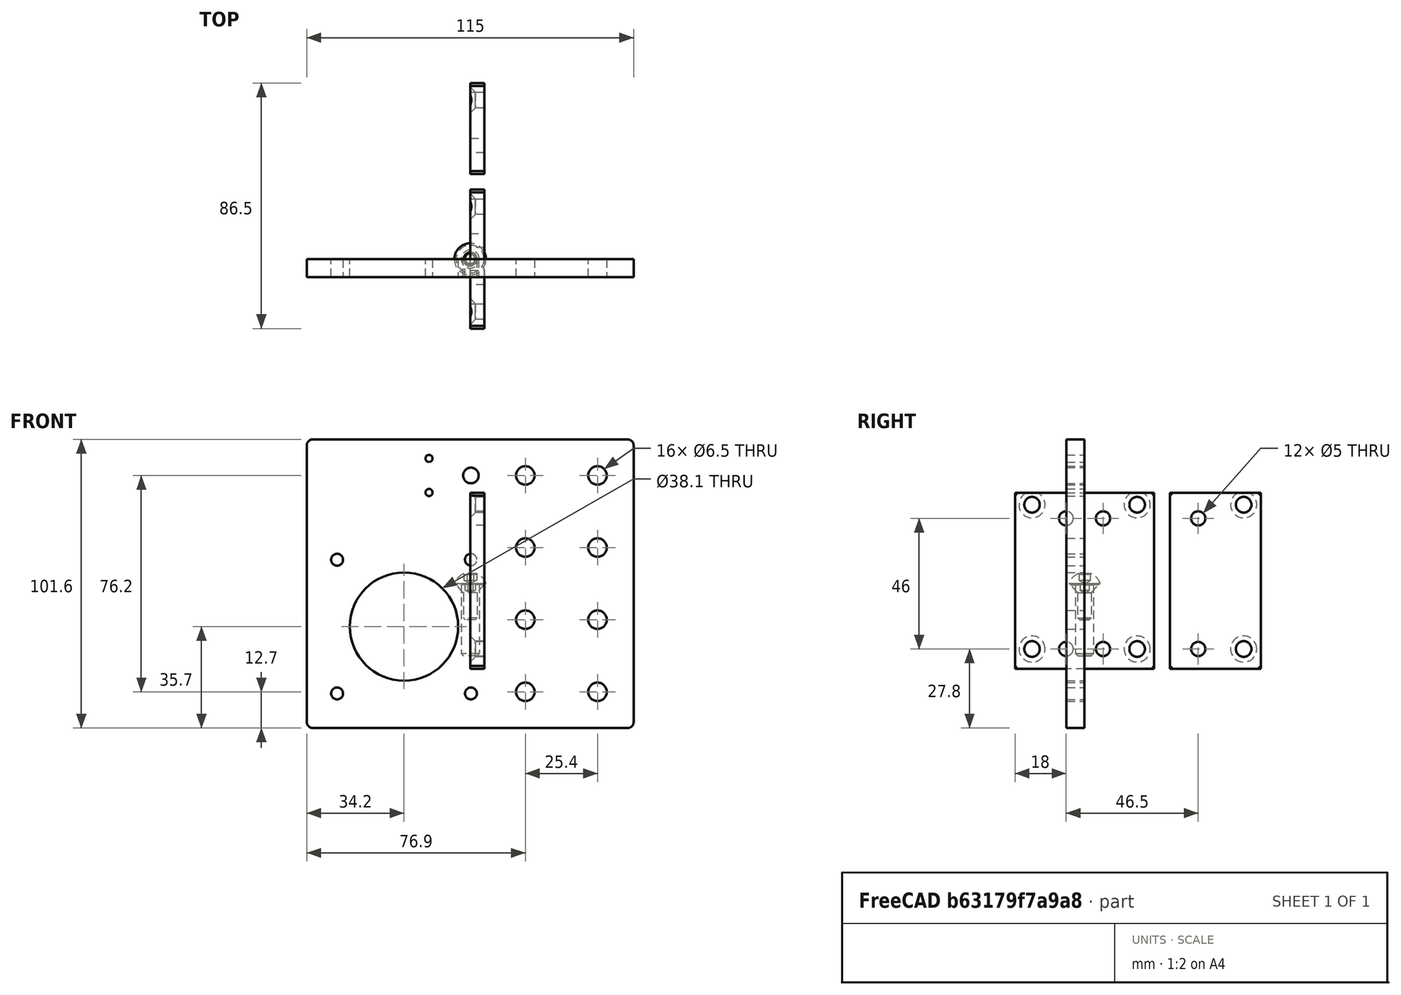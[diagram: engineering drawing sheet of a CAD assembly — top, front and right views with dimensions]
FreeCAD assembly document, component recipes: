
FREECAD ASSEMBLY — COMPONENT RECIPES ("Y axis plates")

This assembly document has 18 components, labeled P0..P17 below (a component is one placed body or linked part). 10 of them carry a construction recipe — the FreeCAD feature program that regenerates the part from scratch, quoted from this document or its linked companion documents; the rest are supplied as boundary geometry only. No exploded tour is included for this assembly.
COMPONENT P0 — recipe-attached ("BK12 plate", modeled in this document).
Construction recipe (the document's own serialized feature program — sketch geometry with constraints, then the solid features built on it; lengths are millimeters unless a unit is written):

FEATURE [Sketcher::SketchObject] Sketch
  FullyConstrained = true
  MapMode = 5
  Placement = pos=(0,0,0) rot=(0.57735,0.57735,0.57735;2.0944rad)
  Support = -> [YZ_Plane]
  sketch-geometry (16):
    g0: LineSegment StartX=-24.5 StartY=32 StartZ=0 EndX=24.5 EndY=32 EndZ=0
    g1: LineSegment StartX=24.5 StartY=32 StartZ=0 EndX=24.5 EndY=-30 EndZ=0
    g2: LineSegment StartX=24.5 StartY=-30 StartZ=0 EndX=-24.5 EndY=-30 EndZ=0
    g3: LineSegment StartX=-24.5 StartY=-30 StartZ=0 EndX=-24.5 EndY=32 EndZ=0
    g4: LineSegment [constr] StartX=-12.5 StartY=30 StartZ=0 EndX=12.5 EndY=30 EndZ=0
    g5: LineSegment [constr] StartX=12.5 StartY=30 StartZ=0 EndX=12.5 EndY=-30 EndZ=0
    g6: LineSegment [constr] StartX=12.5 StartY=-30 StartZ=0 EndX=-12.5 EndY=-30 EndZ=0
    g7: LineSegment [constr] StartX=-12.5 StartY=-30 StartZ=0 EndX=-12.5 EndY=30 EndZ=0
    g8: Circle CenterX=-6.5 CenterY=23 CenterZ=0 NormalX=0 NormalY=0 NormalZ=1 AngleXU=0 Radius=2.5
    g9: Circle CenterX=6.5 CenterY=23 CenterZ=0 NormalX=0 NormalY=0 NormalZ=1 AngleXU=0 Radius=2.5
    g10: Circle CenterX=-6.5 CenterY=-23 CenterZ=0 NormalX=0 NormalY=0 NormalZ=1 AngleXU=0 Radius=2.5
    g11: Circle CenterX=6.5 CenterY=-23 CenterZ=0 NormalX=0 NormalY=0 NormalZ=1 AngleXU=0 Radius=2.5
    g12: Circle CenterX=18.5 CenterY=-23 CenterZ=0 NormalX=0 NormalY=0 NormalZ=1 AngleXU=0 Radius=2.75
    g13: Circle CenterX=18.5 CenterY=27.8 CenterZ=0 NormalX=0 NormalY=0 NormalZ=1 AngleXU=0 Radius=2.75
    g14: Circle CenterX=-18.5 CenterY=27.8 CenterZ=0 NormalX=0 NormalY=0 NormalZ=1 AngleXU=0 Radius=2.75
    g15: Circle CenterX=-18.5 CenterY=-23 CenterZ=0 NormalX=0 NormalY=0 NormalZ=1 AngleXU=0 Radius=2.75
  constraints (44):
    c: Coincident(g0,g1)
    c: Coincident(g1,g2)
    c: Coincident(g2,g3)
    c: Coincident(g3,g0)
    c: Horizontal(g0)
    c: Vertical(g1)
    c: Vertical(g3)
    c: Coincident(g4,g5)
    c: Coincident(g5,g6)
    c: Coincident(g6,g7)
    c: Coincident(g7,g4)
    c: Horizontal(g4)
    c: Horizontal(g6)
    c: Vertical(g5)
    c: Vertical(g7)
    c: Symmetric(g5,g4,g-1)
    c: DistanceY(g5,g5) = 60
    c: DistanceX(g4,g4) = 25
    c: Symmetric(g8,g11,g-1)
    c: Vertical(g8,g10)
    c: Vertical(g9,g11)
    c: Horizontal(g8,g9)
    c: Horizontal(g10,g11)
    c: Equal(g8,g9)
    c: Diameter(g9) = 5
    c: DistanceX(g10,g11) = 13
    c: DistanceY(g11,g9) = 46
    c: Horizontal(g2,g6)
    c: DistanceX(g4,g13) = 6
    c: DistanceX(g13,g0) = 6
    c: DistanceY(g12,g13) = 50.8
    c: Equal(g13,g12)
    c: Diameter(g13) = 5.5
    c: Vertical(g12,g13)
    c: Horizontal(g11,g12)
    c: Symmetric(g1,g2,g-2)
    c: Equal(g15,g14)
    c: Equal(g14,g13)
    c: Horizontal(g14,g13)
    c: Symmetric(g12,g15,g-2)
    c: Vertical(g14,g15)
    c: Equal(g10,g11)
    c: Equal(g10,g8)
    c: DistanceY(g3,g3) = 62
FEATURE [PartDesign::Pad] Pad
  ClaimChildren = false
  Direction = (1,1,1)
  Fit = 0
  FitJoin = 0
  InnerFit = 0
  InnerFitJoin = 0
  InnerTaperAngle = 0
  InnerTaperAngleRev = 0
  Length = 5
  Length2 = 100
  Linearize = true
  NewSolid = false
  Placement = pos=(0,0,0) rot=(0.57735,0.57735,0.57735;2.0944rad)
  Profile = -> Sketch
  Refine = true
  Suppress = false
  Type = 0
  _ProfileBasedVersion = 0
FEATURE [PartDesign::Body] Body  label="BK12 plate"
  AutoGroupSolids = false
  ExportMode = 0
  Group = -> [Sketch,Pad]
  Origin = -> Origin
  Tip = -> Pad
  _ExportChildren = -> [Pad]
  _GroupVersion = 1
COMPONENT P1 — recipe-attached ("BF12 plate", modeled in this document).
Construction recipe (the document's own serialized feature program — sketch geometry with constraints, then the solid features built on it; lengths are millimeters unless a unit is written):

FEATURE [Sketcher::SketchObject] Sketch001
  FullyConstrained = true
  MapMode = 5
  Placement = pos=(0,0,0) rot=(0.57735,0.57735,0.57735;2.0944rad)
  Support = -> [YZ_Plane001]
  sketch-geometry (12):
    g0: LineSegment [constr] StartX=-10 StartY=30 StartZ=0 EndX=10 EndY=30 EndZ=0
    g1: LineSegment [constr] StartX=10 StartY=30 StartZ=0 EndX=10 EndY=-30 EndZ=0
    g2: LineSegment [constr] StartX=10 StartY=-30 StartZ=0 EndX=-10 EndY=-30 EndZ=0
    g3: LineSegment [constr] StartX=-10 StartY=-30 StartZ=0 EndX=-10 EndY=30 EndZ=0
    g4: Circle CenterX=0 CenterY=23 CenterZ=0 NormalX=0 NormalY=0 NormalZ=1 AngleXU=0 Radius=2.5
    g5: Circle CenterX=0 CenterY=-23 CenterZ=0 NormalX=0 NormalY=0 NormalZ=1 AngleXU=0 Radius=2.5
    g6: Circle CenterX=16 CenterY=27.8 CenterZ=0 NormalX=0 NormalY=0 NormalZ=1 AngleXU=0 Radius=2.75
    g7: Circle CenterX=16 CenterY=-23 CenterZ=0 NormalX=0 NormalY=0 NormalZ=1 AngleXU=0 Radius=2.75
    g8: LineSegment StartX=-10 StartY=-30 StartZ=0 EndX=22 EndY=-30 EndZ=0
    g9: LineSegment StartX=22 StartY=-30 StartZ=0 EndX=22 EndY=32 EndZ=0
    g10: LineSegment StartX=22 StartY=32 StartZ=0 EndX=-10 EndY=32 EndZ=0
    g11: LineSegment StartX=-10 StartY=32 StartZ=0 EndX=-10 EndY=-30 EndZ=0
  constraints (33):
    c: Coincident(g0,g1)
    c: Coincident(g1,g2)
    c: Coincident(g2,g3)
    c: Coincident(g3,g0)
    c: Horizontal(g0)
    c: Horizontal(g2)
    c: Vertical(g1)
    c: Vertical(g3)
    c: Symmetric(g1,g0,g-1)
    c: DistanceX(g0,g0) = 20
    c: DistanceY(g1,g1) = 60
    c: PointOnObject(g4,g-2)
    c: Symmetric(g5,g4,g-1)
    c: DistanceY(g5,g4) = 46
    c: Diameter(g4) = 5
    c: Diameter(g7) = 5.5
    c: Equal(g7,g6)
    c: Horizontal(g7,g5)
    c: Vertical(g7,g6)
    c: DistanceY(g7,g6) = 50.8
    c: DistanceX(g0,g6) = 6
    c: Coincident(g8,g9)
    c: Coincident(g9,g10)
    c: Coincident(g10,g11)
    c: Coincident(g11,g8)
    c: Horizontal(g8)
    c: Horizontal(g10)
    c: Vertical(g9)
    c: Vertical(g11)
    c: Coincident(g8,g2)
    c: DistanceX(g6,g9) = 6
    c: Equal(g5,g4)
    c: DistanceY(g9,g9) = 62
FEATURE [PartDesign::Pad] Pad001
  ClaimChildren = false
  Direction = (1,1,1)
  Fit = 0
  FitJoin = 0
  InnerFit = 0
  InnerFitJoin = 0
  InnerTaperAngle = 0
  InnerTaperAngleRev = 0
  Length = 5
  Length2 = 100
  Linearize = true
  NewSolid = false
  Placement = pos=(0,0,0) rot=(0.57735,0.57735,0.57735;2.0944rad)
  Profile = -> Sketch001
  Refine = true
  Suppress = false
  Type = 0
  _ProfileBasedVersion = 0
FEATURE [PartDesign::Body] Body001  label="BF12 plate"
  AutoGroupSolids = false
  ExportMode = 0
  Group = -> [Sketch001,Pad001]
  Origin = -> Origin001
  Placement = pos=(0,40,0) rot=(0,0,1;0rad)
  Tip = -> Pad001
  _ExportChildren = -> [Pad001]
  _GroupVersion = 1
COMPONENT P2 — recipe-attached ("Link(BK12R plate)", modeled in this document).
Construction recipe (the document's own serialized feature program — sketch geometry with constraints, then the solid features built on it; lengths are millimeters unless a unit is written):

FEATURE [PartDesign::SubShapeBinder] BaseFeature002  label="BaseFeature002(BK12 plate)"
  BindCopyOnChange = 0
  BindMode = 0
  ClaimChildren = false
  Context = -> Body004 [BaseFeature002.]
  FillStyle = 0
  Fuse = true
  MakeFace = true
  PartialLoad = false
  Relative = true
  Support = -> [Body]
  _Version = 8
FEATURE [PartDesign::Chamfer] Chamfer002
  Angle = 45
  Base = -> BaseFeature002 [Edge2,Edge1,Edge5,Edge8]
  ChamferType = 0
  FlipDirection = false
  NewSolid = false
  Refine = true
  Size = 1
  Size2 = 1
  SupportTransform = false
  Suppress = false
FEATURE [PartDesign::Hole] Hole002
  BaseFeature = -> Chamfer002
  ClaimChildren = false
  CustomThreadClearance = 0
  Depth = 25
  DepthType = 0
  Diameter = 5.5
  DrillForDepth = false
  DrillPoint = 1
  DrillPointAngle = 118
  Fit = 0
  FitJoin = 0
  HoleCutCountersinkAngle = 90
  HoleCutCustomValues = false
  HoleCutDepth = 0
  HoleCutDiameter = 9.2
  HoleCutType = 2
  InnerFit = 0
  InnerFitJoin = 0
  ModelThread = false
  NewSolid = false
  Profile = -> Chamfer002 [Edge29,Edge32,Edge31,Edge30]
  Refine = true
  Suppress = false
  Tapered = false
  TaperedAngle = 90
  ThreadClass = 0
  ThreadDepth = 23.5
  ThreadDepthType = 0
  ThreadDirection = 0
  ThreadFit = 0
  ThreadSize = 0
  ThreadType = 0
  Threaded = false
  UseCustomThreadClearance = false
  _ProfileBasedVersion = 0
FEATURE [PartDesign::Body] Body004  label="BK12R plate"
  AutoGroupSolids = false
  BaseFeature = -> BaseFeature002
  ExportMode = 0
  Group = -> [BaseFeature002,Chamfer002,Hole002]
  Origin = -> Origin004
  Tip = -> Hole002
  _ExportChildren = -> [BaseFeature002,Hole002]
  _GroupVersion = 1
COMPONENT P3 — recipe-attached ("Link001(BK12L plate)", modeled in this document).
Construction recipe (the document's own serialized feature program — sketch geometry with constraints, then the solid features built on it; lengths are millimeters unless a unit is written):

FEATURE [PartDesign::SubShapeBinder] BaseFeature003  label="BaseFeature003(BK12 plate)"
  BindCopyOnChange = 0
  BindMode = 0
  ClaimChildren = false
  Context = -> Body005 [BaseFeature003.]
  FillStyle = 0
  Fuse = true
  MakeFace = true
  PartialLoad = false
  Relative = true
  Support = -> [Body]
  _Version = 8
FEATURE [PartDesign::Chamfer] Chamfer003
  Angle = 45
  Base = -> BaseFeature003 [Edge2,Edge1,Edge8,Edge5]
  ChamferType = 0
  FlipDirection = false
  NewSolid = false
  Refine = true
  Size = 1
  Size2 = 1
  SupportTransform = false
  Suppress = false
FEATURE [PartDesign::Hole] Hole003
  BaseFeature = -> Chamfer003
  ClaimChildren = false
  CustomThreadClearance = 0
  Depth = 25
  DepthType = 0
  Diameter = 5.5
  DrillForDepth = false
  DrillPoint = 1
  DrillPointAngle = 118
  Fit = 0
  FitJoin = 0
  HoleCutCountersinkAngle = 90
  HoleCutCustomValues = false
  HoleCutDepth = 0
  HoleCutDiameter = 9.2
  HoleCutType = 2
  InnerFit = 0
  InnerFitJoin = 0
  ModelThread = false
  NewSolid = false
  Profile = -> Chamfer003 [Edge12,Edge15,Edge14,Edge13]
  Refine = true
  Reversed = true
  Suppress = false
  Tapered = false
  TaperedAngle = 90
  ThreadClass = 0
  ThreadDepth = 23.5
  ThreadDepthType = 0
  ThreadDirection = 0
  ThreadFit = 0
  ThreadSize = 0
  ThreadType = 0
  Threaded = false
  UseCustomThreadClearance = false
  _ProfileBasedVersion = 0
FEATURE [PartDesign::Body] Body005  label="BK12L plate"
  AutoGroupSolids = false
  BaseFeature = -> BaseFeature003
  ExportMode = 0
  Group = -> [BaseFeature003,Chamfer003,Hole003]
  Origin = -> Origin005
  Tip = -> Hole003
  _ExportChildren = -> [BaseFeature003,Hole003]
  _GroupVersion = 1
COMPONENT P4 — recipe-attached ("Link002(BF12L plate)", modeled in this document).
Construction recipe (the document's own serialized feature program — sketch geometry with constraints, then the solid features built on it; lengths are millimeters unless a unit is written):

FEATURE [PartDesign::SubShapeBinder] BaseFeature001  label="BaseFeature001(BF12 plate)"
  BindCopyOnChange = 0
  BindMode = 0
  ClaimChildren = false
  Context = -> Body003 [BaseFeature001.]
  FillStyle = 0
  Fuse = true
  MakeFace = true
  PartialLoad = false
  Relative = true
  Support = -> [Body001]
  _Version = 8
FEATURE [PartDesign::Chamfer] Chamfer001
  Angle = 45
  Base = -> BaseFeature001 [Edge5,Edge8,Edge2,Edge1]
  ChamferType = 0
  FlipDirection = false
  NewSolid = false
  Refine = true
  Size = 1
  Size2 = 1
  SupportTransform = false
  Suppress = false
FEATURE [PartDesign::Hole] Hole001
  BaseFeature = -> Chamfer001
  ClaimChildren = false
  CustomThreadClearance = 0
  Depth = 25
  DepthType = 0
  Diameter = 5.5
  DrillForDepth = false
  DrillPoint = 1
  DrillPointAngle = 118
  Fit = 0
  FitJoin = 0
  HoleCutCountersinkAngle = 90
  HoleCutCustomValues = false
  HoleCutDepth = 0
  HoleCutDiameter = 9.2
  HoleCutType = 2
  InnerFit = 0
  InnerFitJoin = 0
  ModelThread = false
  NewSolid = false
  Profile = -> Chamfer001 [Edge13,Edge12]
  Refine = true
  Reversed = true
  Suppress = false
  Tapered = false
  TaperedAngle = 90
  ThreadClass = 0
  ThreadDepth = 23.5
  ThreadDepthType = 0
  ThreadDirection = 0
  ThreadFit = 0
  ThreadSize = 0
  ThreadType = 0
  Threaded = false
  UseCustomThreadClearance = false
  _ProfileBasedVersion = 0
FEATURE [PartDesign::Body] Body003  label="BF12L plate"
  AutoGroupSolids = false
  BaseFeature = -> BaseFeature001
  ExportMode = 0
  Group = -> [BaseFeature001,Chamfer001,Hole001]
  Origin = -> Origin003
  Tip = -> Hole001
  _ExportChildren = -> [BaseFeature001,Hole001]
  _GroupVersion = 1
COMPONENT P5 — recipe-attached ("Link003(BF12R plate)", modeled in this document).
Construction recipe (the document's own serialized feature program — sketch geometry with constraints, then the solid features built on it; lengths are millimeters unless a unit is written):

FEATURE [PartDesign::SubShapeBinder] BaseFeature  label="BaseFeature(BF12 plate)"
  BindCopyOnChange = 0
  BindMode = 0
  ClaimChildren = false
  Context = -> Body002 [BaseFeature.]
  FillStyle = 0
  Fuse = true
  MakeFace = true
  PartialLoad = false
  Relative = true
  Support = -> [Body001]
  _Version = 8
FEATURE [PartDesign::Chamfer] Chamfer
  Angle = 45
  Base = -> BaseFeature [Edge5,Edge8,Edge2,Edge1]
  ChamferType = 0
  FlipDirection = false
  NewSolid = false
  Refine = true
  Size = 1
  Size2 = 1
  SupportTransform = false
  Suppress = false
FEATURE [PartDesign::Hole] Hole
  BaseFeature = -> Chamfer
  ClaimChildren = false
  CustomThreadClearance = 0
  Depth = 25
  DepthType = 0
  Diameter = 5.5
  DrillForDepth = false
  DrillPoint = 1
  DrillPointAngle = 118
  Fit = 0
  FitJoin = 0
  HoleCutCountersinkAngle = 90
  HoleCutCustomValues = false
  HoleCutDepth = 0
  HoleCutDiameter = 9.2
  HoleCutType = 2
  InnerFit = 0
  InnerFitJoin = 0
  ModelThread = false
  NewSolid = false
  Profile = -> Chamfer [Edge26,Edge25]
  Refine = true
  Suppress = false
  Tapered = false
  TaperedAngle = 90
  ThreadClass = 0
  ThreadDepth = 23.5
  ThreadDepthType = 0
  ThreadDirection = 0
  ThreadFit = 0
  ThreadSize = 0
  ThreadType = 0
  Threaded = false
  UseCustomThreadClearance = false
  _ProfileBasedVersion = 0
FEATURE [PartDesign::Body] Body002  label="BF12R plate"
  AutoGroupSolids = false
  BaseFeature = -> BaseFeature
  ExportMode = 0
  Group = -> [BaseFeature,Chamfer,Hole]
  Origin = -> Origin002
  Tip = -> Hole
  _ExportChildren = -> [BaseFeature,Hole]
  _GroupVersion = 1
COMPONENT P6 — recipe-attached ("Link004(motor plate)", modeled in this document).
Construction recipe (the document's own serialized feature program — sketch geometry with constraints, then the solid features built on it; lengths are millimeters unless a unit is written):

FEATURE [Sketcher::SketchObject] Sketch002
  FullyConstrained = true
  MapMode = 5
  Placement = pos=(0,0,0) rot=(1,0,0;1.5708rad)
  Support = -> [XZ_Plane006]
  sketch-geometry (23):
    g0: LineSegment StartX=-57.5 StartY=50.8 StartZ=0 EndX=57.5 EndY=50.8 EndZ=0
    g1: LineSegment StartX=57.5 StartY=50.8 StartZ=0 EndX=57.5 EndY=-50.8 EndZ=0
    g2: LineSegment StartX=57.5 StartY=-50.8 StartZ=0 EndX=-57.5 EndY=-50.8 EndZ=0
    g3: LineSegment StartX=-57.5 StartY=-50.8 StartZ=0 EndX=-57.5 EndY=50.8 EndZ=0
    g4: Circle CenterX=19.4 CenterY=38.1 CenterZ=0 NormalX=0 NormalY=0 NormalZ=1 AngleXU=0 Radius=3.25
    g5: Circle CenterX=44.8 CenterY=38.1 CenterZ=0 NormalX=0 NormalY=0 NormalZ=1 AngleXU=0 Radius=3.25
    g6: Circle CenterX=19.4 CenterY=12.7 CenterZ=0 NormalX=0 NormalY=0 NormalZ=1 AngleXU=0 Radius=3.25
    g7: Circle CenterX=44.8 CenterY=12.7 CenterZ=0 NormalX=0 NormalY=0 NormalZ=1 AngleXU=0 Radius=3.25
    g8: Circle CenterX=19.4 CenterY=-12.7 CenterZ=0 NormalX=0 NormalY=0 NormalZ=1 AngleXU=0 Radius=3.25
    g9: Circle CenterX=44.8 CenterY=-12.7 CenterZ=0 NormalX=0 NormalY=0 NormalZ=1 AngleXU=0 Radius=3.25
    g10: Circle CenterX=19.4 CenterY=-38.1 CenterZ=0 NormalX=0 NormalY=0 NormalZ=1 AngleXU=0 Radius=3.25
    g11: Circle CenterX=44.8 CenterY=-38.1 CenterZ=0 NormalX=0 NormalY=0 NormalZ=1 AngleXU=0 Radius=3.25
    g12: LineSegment [constr] StartX=19.4 StartY=38.1 StartZ=0 EndX=44.8 EndY=38.1 EndZ=0
    g13: LineSegment [constr] StartX=19.4 StartY=38.1 StartZ=0 EndX=19.4 EndY=12.7 EndZ=0
    g14: LineSegment [constr] StartX=19.4 StartY=12.7 StartZ=0 EndX=19.4 EndY=-12.7 EndZ=0
    g15: LineSegment [constr] StartX=19.4 StartY=-12.7 StartZ=0 EndX=19.4 EndY=-38.1 EndZ=0
    g16: Circle CenterX=-23.3 CenterY=-15.1 CenterZ=0 NormalX=0 NormalY=0 NormalZ=1 AngleXU=0 Radius=19.05
    g17: Circle CenterX=-46.85 CenterY=8.45 CenterZ=0 NormalX=0 NormalY=0 NormalZ=1 AngleXU=0 Radius=2.1
    g18: Circle CenterX=0.25 CenterY=8.45 CenterZ=0 NormalX=0 NormalY=0 NormalZ=1 AngleXU=0 Radius=2.1
    g19: Circle CenterX=-46.85 CenterY=-38.65 CenterZ=0 NormalX=0 NormalY=0 NormalZ=1 AngleXU=0 Radius=2.1
    g20: Circle CenterX=0.25 CenterY=-38.65 CenterZ=0 NormalX=0 NormalY=0 NormalZ=1 AngleXU=0 Radius=2.1
    g21: LineSegment [constr] StartX=-46.85 StartY=8.45 StartZ=0 EndX=0.25 EndY=8.45 EndZ=0
    g22: LineSegment [constr] StartX=-46.85 StartY=8.45 StartZ=0 EndX=-46.85 EndY=-38.65 EndZ=0
  constraints (56):
    c: Coincident(g0,g1)
    c: Coincident(g1,g2)
    c: Coincident(g2,g3)
    c: Coincident(g3,g0)
    c: Horizontal(g0)
    c: Horizontal(g2)
    c: Vertical(g1)
    c: Vertical(g3)
    c: DistanceX(g0,g0) = 115
    c: DistanceY(g1,g1) = 101.6
    c: Symmetric(g2,g0,g-1)
    c: Diameter(g4) = 6.5
    c: Equal(g4, g5-g9) x5
    c: Equal(g4,g11)
    c: Equal(g4,g10)
    c: Vertical(g4,g6)
    c: Vertical(g8,g10)
    c: Vertical(g5,g7)
    c: Vertical(g7,g9)
    c: Vertical(g9,g11)
    c: Horizontal(g10,g11)
    c: Horizontal(g4,g5)
    c: Horizontal(g6,g7)
    c: Horizontal(g8,g9)
    c: DistanceX(g5,g0) = 12.7
    c: Coincident(g12,g4)
    c: Coincident(g12,g5)
    c: Coincident(g13,g4)
    c: Coincident(g13,g6)
    c: Coincident(g14,g6)
    c: Coincident(g14,g8)
    c: Coincident(g15,g8)
    c: Coincident(g15,g10)
    c: Equal(g15,g14)
    c: Equal(g14,g13)
    c: Equal(g13,g12)
    c: DistanceX(g10,g11) = 25.4
    c: Symmetric(g6,g8,g-1)
    c: Horizontal(g20,g19)
    c: Horizontal(g17,g18)
    c: Vertical(g18,g20)
    c: Vertical(g17,g19)
    c: Diameter(g19) = 4.2
    c: Equal(g19,g20)
    c: Equal(g19,g18)
    c: Equal(g19,g17)
    c: Symmetric(g19,g18,g16)
    c: Diameter(g16) = 38.1
    c: Coincident(g21,g17)
    c: Coincident(g21,g18)
    c: Coincident(g22,g17)
    c: Coincident(g22,g19)
    c: Equal(g22,g21)
    c: DistanceX(g21,g21) = 47.1
    c: DistanceY(g10,g16) = 23
    c: DistanceX(g16,g10) = 42.7
FEATURE [PartDesign::Pad] Pad002
  ClaimChildren = false
  Direction = (1,1,1)
  Fit = 0
  FitJoin = 0
  InnerFit = 0
  InnerFitJoin = 0
  InnerTaperAngle = 0
  InnerTaperAngleRev = 0
  Length = 6.35
  Length2 = 100
  Linearize = true
  NewSolid = false
  Placement = pos=(0,0,0) rot=(1,0,0;1.5708rad)
  Profile = -> Sketch002
  Refine = true
  Suppress = false
  Type = 0
  _ProfileBasedVersion = 0
FEATURE [PartDesign::Fillet] Fillet
  Base = -> Pad002 [Edge2,Edge5,Edge8,Edge1]
  BaseFeature = -> Pad002
  NewSolid = false
  Placement = pos=(0,0,0) rot=(1,0,0;1.5708rad)
  Radius = 2
  Refine = true
  SupportTransform = false
  Suppress = false
FEATURE [Sketcher::SketchObject] Sketch004
  ExternalGeometry = -> [Fillet]
  FullyConstrained = false
  MapMode = 5
  Placement = pos=(0,0,0) rot=(-1,0,0;1.5708rad)
  Support = -> [Fillet]
  sketch-geometry (4):
    g0: Circle CenterX=-14.5 CenterY=-32.1 CenterZ=0 NormalX=0 NormalY=0 NormalZ=1 AngleXU=0 Radius=1.25
    g1: Circle CenterX=-14.5 CenterY=-44.1 CenterZ=0 NormalX=0 NormalY=0 NormalZ=1 AngleXU=0 Radius=1.25
    g2: LineSegment [constr] StartX=60.7569 StartY=-38.1 StartZ=0 EndX=-84.1022 EndY=-38.1 EndZ=0
    g3: Circle CenterX=0.25 CenterY=-38.1 CenterZ=0 NormalX=0 NormalY=0 NormalZ=1 AngleXU=0 Radius=2.75
  constraints (10):
    c: Equal(g0,g1)
    c: Symmetric(g0,g1,g2)
    c: Diameter(g0) = 2.5
    c: DistanceX(g-4,g1) = 43
    c: DistanceY(g1,g0) = 12
    c: PointOnObject(g3,g2)
    c: Diameter(g3) = 5.5
    c: Vertical(g-5,g3)
    c: PointOnObject(g-3,g2)
    c: Horizontal(g2)
FEATURE [PartDesign::Pocket] Pocket
  BaseFeature = -> Fillet
  ClaimChildren = false
  Fit = 0
  FitJoin = 0
  InnerFit = 0
  InnerFitJoin = 0
  InnerTaperAngle = 0
  InnerTaperAngleRev = 0
  Length = 5
  Length2 = 100
  Linearize = true
  NewSolid = false
  Placement = pos=(0,0,0) rot=(1,0,0;1.5708rad)
  Profile = -> Sketch004
  Refine = true
  Suppress = false
  Type = 1
  _ProfileBasedVersion = 1
FEATURE [PartDesign::Body] Body006  label="motor plate"
  AutoGroupSolids = false
  ExportMode = 0
  Group = -> [Sketch002,Pad002,Fillet,Sketch004,Pocket]
  Origin = -> Origin006
  Tip = -> Pocket
  _ExportChildren = -> [Pad002,Fillet,Pocket]
  _GroupVersion = 1
COMPONENT P7 — same part as P6; its construction recipe is shown at P6.
COMPONENT P8 — geometry summary ("1/4inx1in-Screw 8ct"; no construction recipe available for this part):
  bounding box: 87.3 x 36.5 x 28.9 mm
  tessellated surface: 66,304 triangles
  volume: 7853 mm^3 (9% of its bounding box)
  symmetry: 2-fold rotationally symmetric about the y axis; mirror-symmetric across its x mid-plane
COMPONENT P9 — geometry summary ("1/4inx1in-Screw 8ct "; no construction recipe available for this part):
  bounding box: 87.3 x 36.5 x 28.9 mm
  tessellated surface: 66,304 triangles
  volume: 7853 mm^3 (9% of its bounding box)
  symmetry: 2-fold rotationally symmetric about the y axis; mirror-symmetric across its x mid-plane
COMPONENT P10 — geometry summary ("#10x3/8in-Screw 2ct"; no construction recipe available for this part):
  bounding box: 60.6 x 12.7 x 9.8 mm
  tessellated surface: 10,204 triangles
  volume: 596 mm^3 (8% of its bounding box)
  symmetry: 2-fold rotationally symmetric about the x axis; mirror-symmetric across its y mid-plane, z mid-plane
COMPONENT P11 — geometry summary ("#10x3/8in-Screw 4ct"; no construction recipe available for this part):
  bounding box: 60.6 x 46.8 x 12.7 mm
  tessellated surface: 20,408 triangles
  volume: 1191 mm^3 (3% of its bounding box)
  symmetry: mirror-symmetric across its z mid-plane
COMPONENT P12 — geometry summary ("#10x3/8in-Screw 2ct "; no construction recipe available for this part):
  bounding box: 60.6 x 12.7 x 9.8 mm
  tessellated surface: 10,204 triangles
  volume: 596 mm^3 (8% of its bounding box)
  symmetry: 2-fold rotationally symmetric about the x axis; mirror-symmetric across its y mid-plane, z mid-plane
COMPONENT P13 — geometry summary ("#10x3/8in-Screw 4ct "; no construction recipe available for this part):
  bounding box: 60.6 x 46.8 x 12.7 mm
  tessellated surface: 20,408 triangles
  volume: 1191 mm^3 (3% of its bounding box)
  symmetry: mirror-symmetric across its z mid-plane
COMPONENT P14 — recipe-attached ("Link013(front plate)", modeled in this document).
Construction recipe (the document's own serialized feature program — sketch geometry with constraints, then the solid features built on it; lengths are millimeters unless a unit is written):

FEATURE [PartDesign::ShapeBinder] ShapeBinder
  Placement = pos=(0,-6.35,-1.4e-15) rot=(0,0,1;0rad)
  Support = -> [Fillet]
  TraceSupport = false
FEATURE [Sketcher::SketchObject] Sketch003
  ExternalGeometry = -> [ShapeBinder]
  FullyConstrained = true
  MapMode = 5
  Placement = pos=(0,0,0) rot=(1,0,0;1.5708rad)
  Support = -> [XZ_Plane007]
  sketch-geometry (12):
    g0: LineSegment StartX=-57.5 StartY=50.8 StartZ=0 EndX=57.5 EndY=50.8 EndZ=0
    g1: LineSegment StartX=57.5 StartY=50.8 StartZ=0 EndX=57.5 EndY=-50.8 EndZ=0
    g2: LineSegment StartX=57.5 StartY=-50.8 StartZ=0 EndX=-57.5 EndY=-50.8 EndZ=0
    g3: LineSegment StartX=-57.5 StartY=-50.8 StartZ=0 EndX=-57.5 EndY=50.8 EndZ=0
    g4: Circle CenterX=19.4 CenterY=12.7 CenterZ=0 NormalX=0 NormalY=0 NormalZ=1 AngleXU=0 Radius=3.25
    g5: Circle CenterX=44.8 CenterY=12.7 CenterZ=0 NormalX=0 NormalY=0 NormalZ=1 AngleXU=0 Radius=3.25
    g6: Circle CenterX=44.8 CenterY=38.1 CenterZ=0 NormalX=0 NormalY=0 NormalZ=1 AngleXU=0 Radius=3.25
    g7: Circle CenterX=19.4 CenterY=38.1 CenterZ=0 NormalX=0 NormalY=0 NormalZ=1 AngleXU=0 Radius=3.25
    g8: Circle CenterX=19.4 CenterY=-38.1 CenterZ=0 NormalX=0 NormalY=0 NormalZ=1 AngleXU=0 Radius=3.25
    g9: Circle CenterX=19.4 CenterY=-12.7 CenterZ=0 NormalX=0 NormalY=0 NormalZ=1 AngleXU=0 Radius=3.25
    g10: Circle CenterX=44.8 CenterY=-12.7 CenterZ=0 NormalX=0 NormalY=0 NormalZ=1 AngleXU=0 Radius=3.25
    g11: Circle CenterX=44.8 CenterY=-38.1 CenterZ=0 NormalX=0 NormalY=0 NormalZ=1 AngleXU=0 Radius=3.25
  constraints (30):
    c: Coincident(g0,g1)
    c: Coincident(g1,g2)
    c: Coincident(g2,g3)
    c: Coincident(g3,g0)
    c: Horizontal(g0)
    c: Horizontal(g2)
    c: Vertical(g1)
    c: Vertical(g3)
    c: Horizontal(g0,g-3)
    c: Vertical(g0,g-4)
    c: Symmetric(g0,g1,g-1)
    c: Coincident(g4,g-6)
    c: Coincident(g5,g-7)
    c: Coincident(g6,g-8)
    c: Vertical(g11,g10)
    c: Vertical(g10,g6)
    c: Vertical(g4,g7)
    c: Horizontal(g7,g6)
    c: Horizontal(g8,g11)
    c: Horizontal(g9,g10)
    c: Symmetric(g9,g4,g-1)
    c: Symmetric(g7,g8,g-1)
    c: Equal(g4,g5)
    c: Equal(g5,g7)
    c: Equal(g7,g6)
    c: Equal(g6,g8)
    c: Equal(g8,g11)
    c: Equal(g11,g9)
    c: Equal(g9,g10)
    c: Equal(g4,g-6)
FEATURE [PartDesign::Pad] Pad003
  ClaimChildren = false
  Direction = (1,1,1)
  Fit = 0
  FitJoin = 0
  InnerFit = 0
  InnerFitJoin = 0
  InnerTaperAngle = 0
  InnerTaperAngleRev = 0
  Length = 6.35
  Length2 = 100
  Linearize = true
  NewSolid = false
  Placement = pos=(0,0,0) rot=(1,0,0;1.5708rad)
  Profile = -> Sketch003
  Refine = true
  Suppress = false
  Type = 0
  _ProfileBasedVersion = 1
FEATURE [PartDesign::Fillet] Fillet001
  Base = -> Pad003 [Edge1,Edge2,Edge5,Edge8]
  BaseFeature = -> Pad003
  NewSolid = false
  Placement = pos=(0,0,0) rot=(1,0,0;1.5708rad)
  Radius = 2
  Refine = true
  SupportTransform = false
  Suppress = false
FEATURE [PartDesign::Body] Body007  label="front plate"
  AutoGroupSolids = false
  ExportMode = 0
  Group = -> [ShapeBinder,Sketch003,Pad003,Fillet001]
  Origin = -> Origin007
  Tip = -> Fillet001
  _ExportChildren = -> [ShapeBinder,Pad003,Fillet001]
  _GroupVersion = 1
COMPONENT P15 — same part as P14; its construction recipe is shown at P14.
COMPONENT P16 — geometry summary ("1/4inx1in-Screw 8ct      "; no construction recipe available for this part):
  bounding box: 87.3 x 36.5 x 28.9 mm
  tessellated surface: 66,304 triangles
  volume: 7853 mm^3 (9% of its bounding box)
  symmetry: 2-fold rotationally symmetric about the y axis; mirror-symmetric across its x mid-plane
COMPONENT P17 — geometry summary ("1/4inx1in-Screw 8ct    "; no construction recipe available for this part):
  bounding box: 87.3 x 36.5 x 28.9 mm
  tessellated surface: 66,304 triangles
  volume: 7853 mm^3 (9% of its bounding box)
  symmetry: 2-fold rotationally symmetric about the y axis; mirror-symmetric across its x mid-plane
PROVENANCE & LICENSES
A FreeCAD (.FCStd) document from a public repository crawl; recipes are the document's own serialized feature recipes (and, for linked parts, companion documents' recipes).
License: mit.
